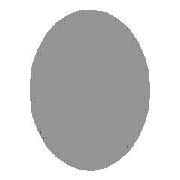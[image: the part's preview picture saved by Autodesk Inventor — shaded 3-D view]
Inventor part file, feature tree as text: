
AUTODESK INVENTOR PART (.ipt)
format: ipt  version: 2025.1 (Build 291241020, 241B)  size: 103,936 bytes
history: native  units: mm (DEFAULTED — no unit token found)
features: other x3, sketch x1, plane x1
ambient origin geometry x8: Origin, YZ Plane, XZ Plane, XY Plane, X Axis, Y Axis, Z Axis, Center Point
bodies: Solid1 (feature_tree), Body (feature_tree)
feature tree (5):
  other  "Driven Length"
  other  "Start plane"
  other  "End plane"
  sketch  "Sketch3"  dims[d1=2800.0mm d2=0.0mm d4=-0.0mm d5=2800.0mm d0=16.0mm d7=90.0deg d8=2800.0mm]
  plane  "Work Plane3"
